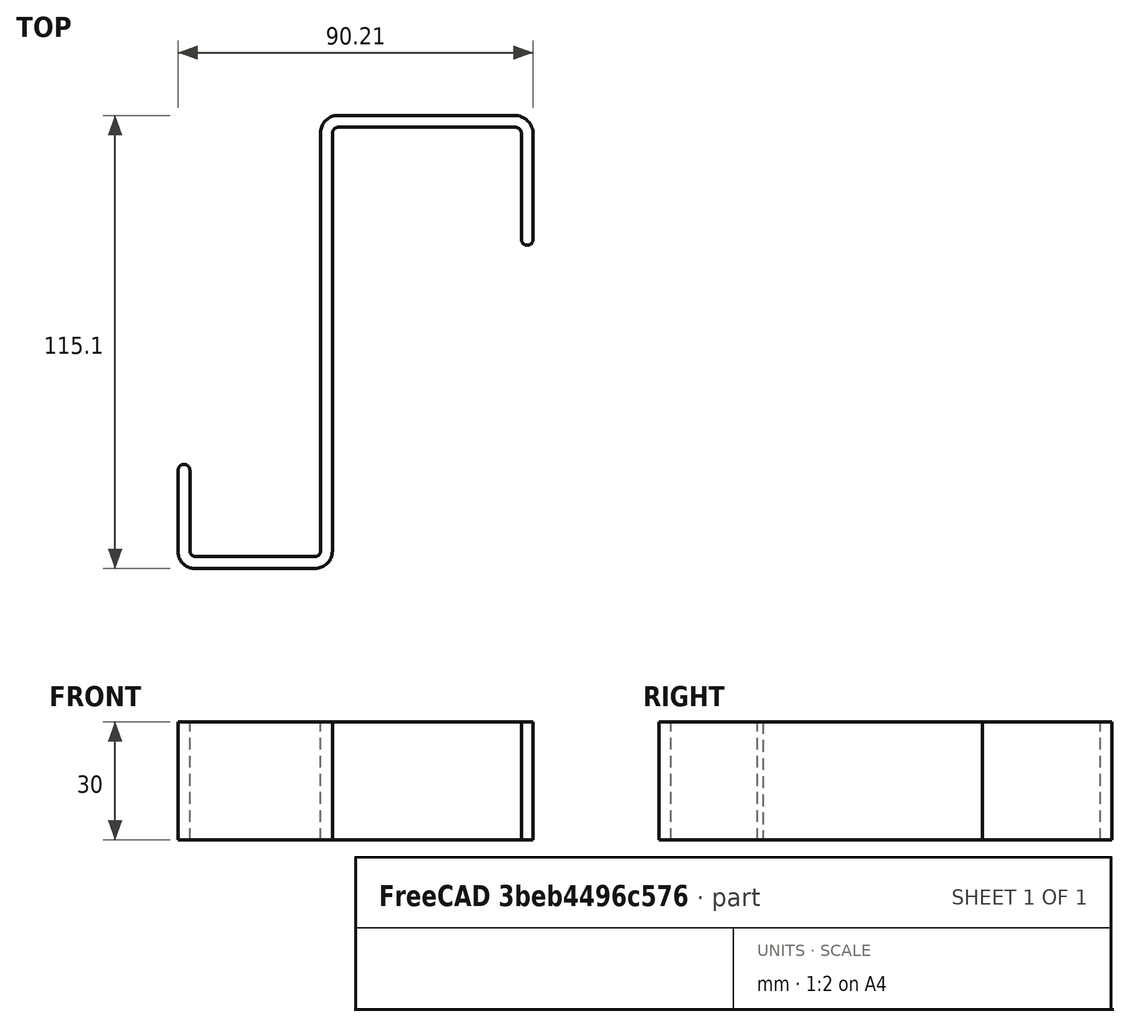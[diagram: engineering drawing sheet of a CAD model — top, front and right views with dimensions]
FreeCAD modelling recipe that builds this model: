
FCSTD DOCUMENT  (FreeCAD 1.0R39109 (Git))
Label: ColgadorPuerta
License: All rights reserved
LicenseURL: http://en.wikipedia.org/wiki/All_rights_reserved
objects: Sketcher::SketchObject×1, PartDesign::Pad×1, PartDesign::Body×1
note: 6 computed .brp shape members not serialized (recipe doc carries the construction recipe); baked Part::Feature solids carry a one-line shape summary decoded from their .brp

FEATURE [Sketcher::SketchObject] Sketch
  ArcFitTolerance = 1e-06
  AttachmentSupport = -> [XY_Plane]
  FullyConstrained = false
  MakeInternals = false
  MapMode = 5
  sketch-geometry (30):
    g0: LineSegment StartX=54 StartY=22.9096 StartZ=0 EndX=54 EndY=49.6015 EndZ=0
    g1: LineSegment StartX=49.2006 StartY=54.4009 StartZ=0 EndX=4.4095 EndY=54.4009 EndZ=0
    g2: LineSegment StartX=0 StartY=49.9915 StartZ=0 EndX=0 EndY=-56.1973 EndZ=0
    g3: LineSegment StartX=-1.5 StartY=-57.6973 StartZ=0 EndX=-31.7109 EndY=-57.6973 EndZ=0
    g4: LineSegment StartX=-33.2109 StartY=-56.1973 StartZ=0 EndX=-33.2109 EndY=-35.7742 EndZ=0
    g5: LineSegment [constr] StartX=54 StartY=22.9096 StartZ=0 EndX=51 EndY=22.9096 EndZ=0
    g6: LineSegment StartX=51 StartY=22.9096 StartZ=0 EndX=51 EndY=49.9009 EndZ=0
    g7: LineSegment StartX=49.5 StartY=51.4009 StartZ=0 EndX=4.5 EndY=51.4009 EndZ=0
    g8: LineSegment StartX=3 StartY=49.9009 StartZ=0 EndX=3 EndY=-56.2789 EndZ=0
    g9: LineSegment StartX=-1.41841 StartY=-60.6973 StartZ=0 EndX=-32.0201 EndY=-60.6973 EndZ=0
    g10: LineSegment StartX=-36.2109 StartY=-56.5066 StartZ=0 EndX=-36.2109 EndY=-35.7741 EndZ=0
    g11: LineSegment StartX=-33.2109 StartY=-35.7742 StartZ=0 EndX=-33.2109 EndY=-35.7742 EndZ=0
    g12: ArcOfCircle CenterX=-34.7109 CenterY=-35.7653 CenterZ=0 NormalX=0 NormalY=0 NormalZ=1 AngleXU=0 Radius=1.5 StartAngle=6.27725 EndAngle=9.43062
    g13: ArcOfCircle CenterX=52.5 CenterY=22.9096 CenterZ=0 NormalX=0 NormalY=0 NormalZ=1 AngleXU=0 Radius=1.5 StartAngle=3.14159 EndAngle=6.28319
    g14: ArcOfCircle CenterX=49.5 CenterY=49.9009 CenterZ=0 NormalX=0 NormalY=0 NormalZ=1 AngleXU=0 Radius=1.5 StartAngle=2.1e-15 EndAngle=1.5708
    g15: GeomPoint [constr] X=51 Y=51.4009 Z=0
    g16: ArcOfCircle CenterX=4.5 CenterY=49.9009 CenterZ=0 NormalX=0 NormalY=0 NormalZ=1 AngleXU=0 Radius=1.5 StartAngle=1.5708 EndAngle=3.14159
    g17: GeomPoint [constr] X=3 Y=51.4009 Z=0
    g18: ArcOfCircle CenterX=49.2006 CenterY=49.6015 CenterZ=0 NormalX=0 NormalY=0 NormalZ=1 AngleXU=0 Radius=4.79942 StartAngle=0 EndAngle=1.5708
    g19: GeomPoint [constr] X=54 Y=54.4009 Z=0
    g20: ArcOfCircle CenterX=4.4095 CenterY=49.9915 CenterZ=0 NormalX=0 NormalY=0 NormalZ=1 AngleXU=0 Radius=4.4095 StartAngle=1.5708 EndAngle=3.14159
    g21: GeomPoint [constr] X=0 Y=54.4009 Z=0
    g22: ArcOfCircle CenterX=-1.5 CenterY=-56.1973 CenterZ=0 NormalX=0 NormalY=0 NormalZ=1 AngleXU=0 Radius=1.5 StartAngle=4.71239 EndAngle=6.28319
    g23: GeomPoint [constr] X=0 Y=-57.6973 Z=0
    g24: ArcOfCircle CenterX=-1.41841 CenterY=-56.2789 CenterZ=0 NormalX=0 NormalY=0 NormalZ=1 AngleXU=0 Radius=4.41841 StartAngle=4.71239 EndAngle=6.28319
    g25: GeomPoint [constr] X=3 Y=-60.6973 Z=0
    g26: ArcOfCircle CenterX=-31.7109 CenterY=-56.1973 CenterZ=0 NormalX=0 NormalY=0 NormalZ=1 AngleXU=0 Radius=1.5 StartAngle=3.14159 EndAngle=4.71239
    g27: GeomPoint [constr] X=-33.2109 Y=-57.6973 Z=0
    g28: ArcOfCircle CenterX=-32.0201 CenterY=-56.5066 CenterZ=0 NormalX=0 NormalY=0 NormalZ=1 AngleXU=0 Radius=4.19074 StartAngle=3.14159 EndAngle=4.71239
    g29: GeomPoint [constr] X=-36.2109 Y=-60.6973 Z=0
  constraints (64):
    c: Vertical(g0)
    c: PointOnObject(g21,g-2)
    c: Horizontal(g1)
    c: PointOnObject(g23,g-2)
    c: Horizontal(g3)
    c: Vertical(g4)
    c: Coincident(g0,g5)
    c: Coincident(g5,g6)
    c: Vertical(g6)
    c: Horizontal(g7)
    c: Vertical(g8)
    c: Horizontal(g9)
    c: Vertical(g10)
    c: Coincident(g11,g4)
    c: Horizontal(g11)
    c: Horizontal(g5)
    c: Distance(g17,g15) = 48
    c: DistanceX(g15,g19) = 3
    c: DistanceX(g21,g17) = 3
    c: DistanceY(g17,g21) = 3
    c: DistanceX(g29,g27) = 3
    c: DistanceY(g29,g27) = 3
    c: Coincident(g12,g10)
    c: Coincident(g12,g11)
    c: Radius(g12) = 1.5
    c: Coincident(g13,g5)
    c: Coincident(g13,g0)
    c: Radius(g13) = 1.5
    c: PointOnObject(g15,g7)
    c: PointOnObject(g15,g6)
    c: Tangent(g7,g14) = -1.5708
    c: Tangent(g6,g14) = -1.5708
    c: Radius(g14) = 1.5
    c: PointOnObject(g17,g7)
    c: PointOnObject(g17,g8)
    c: Tangent(g7,g16) = -1.5708
    c: Tangent(g8,g16) = -1.5708
    c: Radius(g16) = 1.5
    c: PointOnObject(g19,g1)
    c: PointOnObject(g19,g0)
    c: Tangent(g1,g18) = -1.5708
    c: Tangent(g0,g18) = -1.5708
    c: PointOnObject(g21,g1)
    c: PointOnObject(g21,g2)
    c: Tangent(g1,g20) = -1.5708
    c: Tangent(g2,g20) = -1.5708
    c: PointOnObject(g23,g2)
    c: PointOnObject(g23,g3)
    c: Tangent(g2,g22) = 1.5708
    c: Tangent(g3,g22) = 1.5708
    c: Radius(g22) = 1.5
    c: PointOnObject(g25,g8)
    c: PointOnObject(g25,g9)
    c: Tangent(g8,g24) = 1.5708
    c: Tangent(g9,g24) = 1.5708
    c: PointOnObject(g27,g3)
    c: PointOnObject(g27,g4)
    c: Tangent(g3,g26) = 1.5708
    c: Tangent(g4,g26) = 1.5708
    c: Radius(g26) = 1.5
    c: PointOnObject(g29,g9)
    c: PointOnObject(g29,g10)
    c: Tangent(g9,g28) = 1.5708
    c: Tangent(g10,g28) = 1.5708
FEATURE [PartDesign::Pad] Pad
  Direction = (0,0,1)
  Length = 30
  Length2 = 10
  Profile = -> Sketch
  ReferenceAxis = -> Sketch [N_Axis]
  Suppressed = false
  Type = 0
FEATURE [PartDesign::Body] Body
  AllowCompound = false
  Group = -> [Sketch,Pad]
  Origin = -> Origin
  Tip = -> Pad
